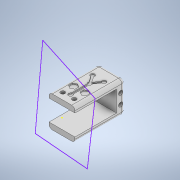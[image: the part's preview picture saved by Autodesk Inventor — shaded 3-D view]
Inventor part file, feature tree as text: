
AUTODESK INVENTOR PART (.ipt)
format: ipt  version: 2022 (Build 260153000, 153)  size: 425,984 bytes
history: native  units: in
note: dims shown in document units (in); Inventor stores cm internally (conversion verified against a paired STEP export)
features: extrude x13, sketch x13, projected_geometry x9, mirror x3, fillet x1
ambient origin geometry x8: Origin, YZ Plane, XZ Plane, XY Plane, X Axis, Y Axis, Z Axis, Center Point
bodies: Solid1 (feature_tree)
feature tree (39):
  extrude  "Extrusion1"  Depth=0.61in
  extrude  "Extrusion2"  Depth=2.5in TaperAngle=0.0deg
  extrude  "Extrusion3"  Depth=0.75in TaperAngle=0.0deg
  extrude  "Extrusion4"  Depth=2.25in
  sketch  "Sketch4"  dims[d5=0.18in d6=0.75in d7=0.0in]
  extrude  "Extrusion6"  Depth=1.6in
  extrude  "Extrusion7"  Depth=1.0in
  extrude  "Extrusion8"  Depth=0.157in
  mirror  "Mirror1"
  fillet  "Fillet4"  Radius=0.2362in
  sketch  "Sketch9"  dims[d17=0.195in d18=0.157in d19=0.2362in]
  extrude  "Extrusion9"  Depth=0.0984in
  extrude  "Extrusion10"  TaperAngle=0.0deg  [1 undecoded]
  extrude  "Extrusion11"  Depth=0.325in TaperAngle=0.0deg
  mirror  "Mirror2"
  extrude  "Extrusion12"  Depth=1.0in TaperAngle=0.0deg
  mirror  "Mirror3"
  sketch  "Sketch12"  dims[d25=1.5748in d28=0.325in d29=0.0in]
  sketch  "Sketch14"  dims[d30=1.0in d31=0.0in d32=0.195in d33=0.0in]
  extrude  "Extrusion14"  Depth=1.3in TaperAngle=0.0deg
  extrude  "Extrusion15"  Depth=0.25in
  sketch  "Sketch1"  dims[d0=0.61in d1=0.61in]
  sketch  "Sketch2"  dims[d2=0.61in d3=2.5in d4=0.0in]
  projected_geometry  "Projected Loop1"
  sketch  "Sketch5"  dims[d9=1.2in d10=2.25in]
  projected_geometry  "Projected Loop2"
  sketch  "Sketch6"  dims[d11=1.6in d12=0.8in]
  projected_geometry  "Projected Loop3"
  sketch  "Sketch7"  dims[d13=1.0in d14=0.0in d16=0.957in]
  projected_geometry  "Projected Loop4"
  projected_geometry  "Projected Loop5"
  sketch  "Sketch10"  dims[d20=0.0984in d21=0.0984in]
  sketch  "Sketch11"  dims[d22=2.25in d23=0.0in]
  projected_geometry  "Projected Loop6"
  projected_geometry  "Projected Loop7"
  sketch  "Sketch15"  dims[d35=0.125in d36=1.3in d37=0.0in]
  projected_geometry  "Projected Loop9"
  sketch  "Sketch16"  dims[d38=2.3in d39=0.0in d40=0.25in d41=0.157in d42=0.22in d43=0.125in d44=0.0in d45=0.1575in d46=0.1575in d47=0.1575in d48=0.1575in d49=0.7425in d54=0.0394in d55=0.0in d56=0.6in d57=0.2125in d61=0.12in d62=0.12in d63=0.25in d64=0.0in d65=0.25in d66=0.0in]
  projected_geometry  "Projected Loop10"
note: 1 required parameter value undecoded (feature->parameter linkage not recoverable at this tier; creation-order binding heuristic only, values carry confidence <= 0.55)
